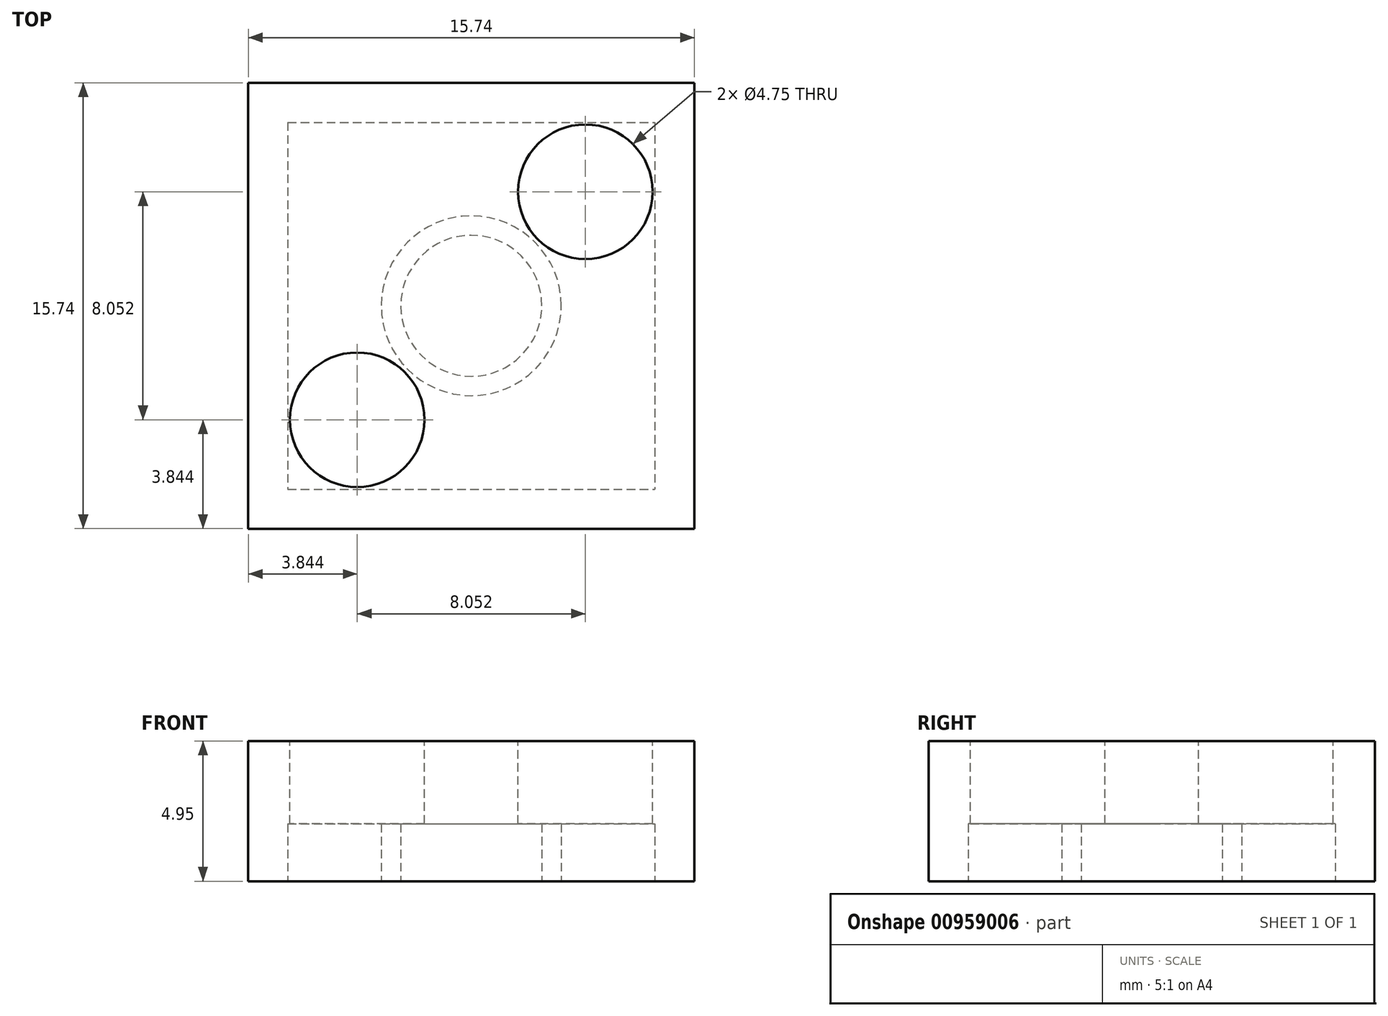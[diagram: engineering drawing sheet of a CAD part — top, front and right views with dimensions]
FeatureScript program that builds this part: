
annotation { "Feature Type Name" : "Feature", "Feature Type Description" : "" }
export const myFeature = defineFeature(function(context is Context, id is Id, definition is map)
    precondition{}
    {
        {
            var Q0;
            Q0=qCreatedBy(makeId("Top.planeOp"),FACE);
            var sketch = newSketch(context, id + "F0", { "sketchPlane" : qUnion([Q0])});
            skLineSegment(sketch, "E0.bottom", {"start": v(7.87, 7.87) * mm, "end": v(-7.87, 7.87) * mm});
            skLineSegment(sketch, "E0.top", {"start": v(7.87, -7.87) * mm, "end": v(-7.87, -7.87) * mm});
            skLineSegment(sketch, "E0.left", {"start": v(7.87, 7.87) * mm, "end": v(7.87, -7.87) * mm});
            skLineSegment(sketch, "E0.right", {"start": v(-7.87, 7.87) * mm, "end": v(-7.87, -7.87) * mm});
            skPoint(sketch, "E0.middle", {"position": v(0, 0) * mm});
            skLineSegment(sketch, "E1.bottom", {"start": v(6.4, 6.4) * mm, "end": v(-6.4, 6.4) * mm, "construction": true});
            skLineSegment(sketch, "E1.top", {"start": v(6.4, -6.4) * mm, "end": v(-6.4, -6.4) * mm, "construction": true});
            skLineSegment(sketch, "E1.left", {"start": v(6.4, 6.4) * mm, "end": v(6.4, -6.4) * mm, "construction": true});
            skLineSegment(sketch, "E1.right", {"start": v(-6.4, 6.4) * mm, "end": v(-6.4, -6.4) * mm, "construction": true});
            skCircle(sketch, "E2", {"center": v(-4.03, 4.03) * mm, "radius": 2.37 * mm});
            skLineSegment(sketch, "E3", {"start": v(0, 6.4) * mm, "end": v(0, -6.4) * mm, "construction": true});
            skLineSegment(sketch, "E4", {"start": v(-6.4, 0) * mm, "end": v(6.4, 0) * mm, "construction": true});
            skLineSegment(sketch, "E5.MirrorCS", {"start": v(6.4, 0) * mm, "end": v(-6.4, 0) * mm, "construction": true});
            skCircle(sketch, "E6.MirrorC", {"center": v(4.03, 4.03) * mm, "radius": 2.37 * mm});
            skCircle(sketch, "E7.MirrorC", {"center": v(-4.03, -4.03) * mm, "radius": 2.37 * mm});
            skCircle(sketch, "E8.MirrorC", {"center": v(4.03, -4.03) * mm, "radius": 2.37 * mm});
            skSolve(sketch);
        }
        {
            var Q0;
            Q0=makeQuery(id+"F0.imprint","IMPRINT",FACE,{"disambiguationData":[TD([[makeQuery(id+"F0.imprint","IMPRINT",EDGE,{"derivedFrom":sQuery(id+"F0.wireOp",EDGE,"E0.bottom")}),1.0]])]});
            var Q1;
            Q1=makeQuery(id+"F0.imprint","IMPRINT",FACE,{"disambiguationData":[TD([[makeQuery(id+"F0.imprint","IMPRINT",EDGE,{"derivedFrom":sQuery(id+"F0.wireOp",EDGE,"E2")}),1.0]])]});
            var Q2;
            Q2=makeQuery(id+"F0.imprint","IMPRINT",FACE,{"disambiguationData":[TD([[makeQuery(id+"F0.imprint","IMPRINT",EDGE,{"derivedFrom":sQuery(id+"F0.wireOp",EDGE,"E7.MirrorC")}),-1.0]])]});
            var Q3;
            Q3=makeQuery(id+"F0.imprint","IMPRINT",FACE,{"disambiguationData":[TD([[makeQuery(id+"F0.imprint","IMPRINT",EDGE,{"derivedFrom":sQuery(id+"F0.wireOp",EDGE,"E8.MirrorC")}),1.0]])]});
            var Q4;
            Q4=makeQuery(id+"F0.imprint","IMPRINT",FACE,{"disambiguationData":[TD([[makeQuery(id+"F0.imprint","IMPRINT",EDGE,{"derivedFrom":sQuery(id+"F0.wireOp",EDGE,"E6.MirrorC")}),-1.0]])]});
            var Q5;
            Q5=sQuery(id+"F0.wireOp",EDGE,"E1.bottom");
            var Q6;
            Q6=sQuery(id+"F0.wireOp",EDGE,"E1.right");
            var Q7;
            Q7=sQuery(id+"F0.wireOp",EDGE,"E1.top");
            var Q8;
            Q8=sQuery(id+"F0.wireOp",EDGE,"E1.left");
            extrude(context, id + "F1", {"entities" : qUnion([Q0, Q1, Q2, Q3, Q4]), "surfaceEntities" : qUnion([Q5, Q6, Q7, Q8]), "oppositeDirection" : true, "depth" : 3.12 * mm, "offsetDistance" : 25.4 * mm});
        }
        {
            var Q0;
            Q0=makeQuery(id+"F0.imprint","IMPRINT",FACE,{"disambiguationData":[TD([[makeQuery(id+"F0.imprint","IMPRINT",EDGE,{"derivedFrom":sQuery(id+"F0.wireOp",EDGE,"E2")}),1.0]])]});
            var Q1;
            Q1=makeQuery(id+"F0.imprint","IMPRINT",FACE,{"disambiguationData":[TD([[makeQuery(id+"F0.imprint","IMPRINT",EDGE,{"derivedFrom":sQuery(id+"F0.wireOp",EDGE,"E7.MirrorC")}),-1.0]])]});
            var Q2;
            Q2=makeQuery(id+"F0.imprint","IMPRINT",FACE,{"disambiguationData":[TD([[makeQuery(id+"F0.imprint","IMPRINT",EDGE,{"derivedFrom":sQuery(id+"F0.wireOp",EDGE,"E8.MirrorC")}),1.0]])]});
            var Q3;
            Q3=makeQuery(id+"F0.imprint","IMPRINT",FACE,{"disambiguationData":[TD([[makeQuery(id+"F0.imprint","IMPRINT",EDGE,{"derivedFrom":sQuery(id+"F0.wireOp",EDGE,"E6.MirrorC")}),-1.0]])]});
            extrude(context, id + "F2", {"entities" : qUnion([Q0, Q1, Q2, Q3]), "operationType" : NewBodyOperationType.ADD, "depth" : 1.83 * mm, "offsetDistance" : 25.4 * mm});
        }
        {
            var Q0;
            Q0=makeQuery(id+"F1.opExtrude","CAP_FACE",FACE,{"disambiguationData":[OSD([sQuery(id+"F0.wireOp",EDGE,"E0.bottom"),sQuery(id+"F0.wireOp",EDGE,"E0.top"),sQuery(id+"F0.wireOp",EDGE,"E0.left"),sQuery(id+"F0.wireOp",EDGE,"E0.right")])],"isStart":false});
            var sketch = newSketch(context, id + "F3", { "sketchPlane" : qUnion([Q0])});
            skCircle(sketch, "E9", {"center": v(0, 0) * mm, "radius": 2.49 * mm});
            skCircle(sketch, "E10", {"center": v(0, 0) * mm, "radius": 3.18 * mm});
            skLineSegment(sketch, "E11.bottom", {"start": v(-6.48, -6.48) * mm, "end": v(6.48, -6.48) * mm});
            skLineSegment(sketch, "E11.top", {"start": v(-6.48, 6.48) * mm, "end": v(6.48, 6.48) * mm});
            skLineSegment(sketch, "E11.left", {"start": v(-6.48, -6.48) * mm, "end": v(-6.48, 6.48) * mm});
            skLineSegment(sketch, "E11.right", {"start": v(6.48, -6.48) * mm, "end": v(6.48, 6.48) * mm});
            skSolve(sketch);
        }
        {
            var Q0;
            Q0=makeQuery(id+"F3.imprint","IMPRINT",FACE,{"disambiguationData":[TD([[makeQuery(id+"F3.imprint","IMPRINT",EDGE,{"derivedFrom":sQuery(id+"F3.wireOp",EDGE,"E10")}),-1.0]])]});
            extrude(context, id + "F4", {"entities" : qUnion([Q0]), "operationType" : NewBodyOperationType.REMOVE, "oppositeDirection" : true, "depth" : 2.03 * mm, "offsetDistance" : 25.4 * mm});
        }
        {
            var Q0;
            Q0=makeQuery(id+"F3.imprint","IMPRINT",FACE,{"disambiguationData":[TD([[makeQuery(id+"F3.imprint","IMPRINT",EDGE,{"derivedFrom":sQuery(id+"F3.wireOp",EDGE,"E9")}),1.0]])]});
            extrude(context, id + "F5", {"entities" : qUnion([Q0]), "operationType" : NewBodyOperationType.REMOVE, "oppositeDirection" : true, "depth" : 2.03 * mm, "offsetDistance" : 25.4 * mm});
        }
    });
